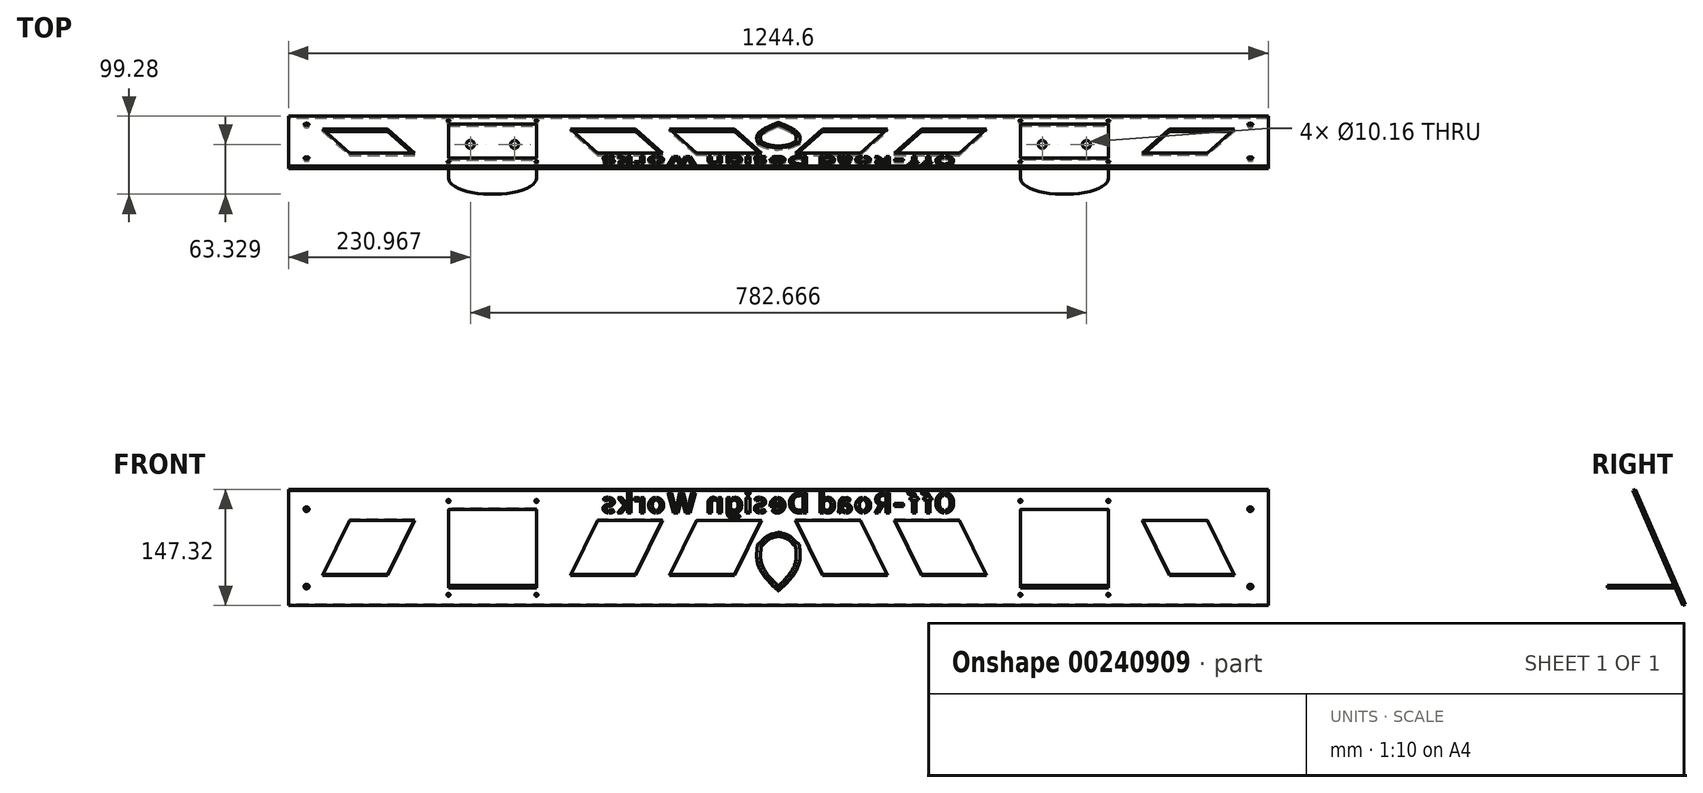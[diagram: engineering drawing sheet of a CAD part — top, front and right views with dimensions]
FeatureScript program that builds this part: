
annotation { "Feature Type Name" : "Feature", "Feature Type Description" : "" }
export const myFeature = defineFeature(function(context is Context, id is Id, definition is map)
    precondition{}
    {
        {
            var Q0;
            Q0=qCreatedBy(makeId("Right.planeOp"),FACE);
            var sketch = newSketch(context, id + "F0", { "sketchPlane" : qUnion([Q0])});
            skLineSegment(sketch, "E0", {"start": v(0, 0) * mm, "end": v(-63.5, 146.05) * mm});
            skLineSegment(sketch, "E1", {"start": v(-63.5, 146.05) * mm, "end": v(-66.41, 144.78) * mm});
            skLineSegment(sketch, "E2", {"start": v(-66.41, 144.78) * mm, "end": v(-2.91, -1.27) * mm});
            skLineSegment(sketch, "E3", {"start": v(-2.91, -1.27) * mm, "end": v(0, 0) * mm});
            skSolve(sketch);
        }
        {
            var Q0;
            Q0=qSketchRegion(id+"F0",true);
            extrude(context, id + "F1", {"entities" : qUnion([Q0]), "depth" : 622.3 * mm, "hasSecondDirection" : true, "secondDirectionOppositeDirection" : true, "secondDirectionDepth" : 622.3 * mm});
        }
        {
            var Q0;
            Q0=makeQuery(id+"F1.opExtrude","SWEPT_FACE",FACE,{"disambiguationData":[OSD([sQuery(id+"F0.wireOp",EDGE,"E0")])]});
            var sketch = newSketch(context, id + "F2", { "sketchPlane" : qUnion([Q0])});
            skSolve(sketch);
        }
        {
            var Q0;
            {var subQ0=sQuery(id+"F0.wireOp",EDGE,"E0");Q0=makeQuery(id+"F2.imprint","IMPRINT",FACE,{"disambiguationData":[TD([[makeQuery(id+"F2.imprint","IMPRINT",EDGE,{"derivedFrom":makeQuery(id+"F1.opExtrude","CAP_EDGE",EDGE,{"disambiguationData":[OSD([subQ0])],"isStart":true})}),1.0]])]});}
            var sketch = newSketch(context, id + "F3", { "sketchPlane" : qUnion([Q0])});
            skLineSegment(sketch, "E4", {"start": v(0, 0) * mm, "end": v(0, -192.6) * mm, "construction": true});
            skLineSegment(sketch, "E5", {"start": v(-307.34, 133.22) * mm, "end": v(-419.1, 133.22) * mm});
            skLineSegment(sketch, "E6", {"start": v(-419.1, 133.22) * mm, "end": v(-419.1, 26.03) * mm});
            skLineSegment(sketch, "E7", {"start": v(-419.1, 26.03) * mm, "end": v(-307.34, 26.03) * mm});
            skLineSegment(sketch, "E8", {"start": v(-307.34, 26.03) * mm, "end": v(-307.34, 133.22) * mm});
            skLineSegment(sketch, "E9", {"start": v(-462.28, 117.73) * mm, "end": v(-544.83, 117.73) * mm});
            skLineSegment(sketch, "E10", {"start": v(-544.83, 117.73) * mm, "end": v(-579.12, 41.53) * mm});
            skLineSegment(sketch, "E11", {"start": v(-579.12, 41.53) * mm, "end": v(-496.57, 41.53) * mm});
            skLineSegment(sketch, "E12", {"start": v(-496.57, 41.53) * mm, "end": v(-462.28, 117.73) * mm});
            skLineSegment(sketch, "E13", {"start": v(-229.87, 117.73) * mm, "end": v(-147.32, 117.73) * mm});
            skLineSegment(sketch, "E14", {"start": v(-147.32, 117.73) * mm, "end": v(-181.6, 41.53) * mm});
            skLineSegment(sketch, "E15", {"start": v(-181.6, 41.53) * mm, "end": v(-264.16, 41.53) * mm});
            skLineSegment(sketch, "E16", {"start": v(-264.16, 41.53) * mm, "end": v(-229.87, 117.73) * mm});
            skLineSegment(sketch, "E17.1.0.0", {"start": v(-21.59, 117.73) * mm, "end": v(-55.88, 41.53) * mm});
            skLineSegment(sketch, "E17.1.0.1", {"start": v(-55.88, 41.53) * mm, "end": v(-138.43, 41.53) * mm});
            skLineSegment(sketch, "E17.1.0.2", {"start": v(-138.43, 41.53) * mm, "end": v(-104.14, 117.73) * mm});
            skLineSegment(sketch, "E17.1.0.3", {"start": v(-104.14, 117.73) * mm, "end": v(-21.59, 117.73) * mm});
            skLineSegment(sketch, "E17.direction1", {"start": v(-229.87, 117.73) * mm, "end": v(-104.14, 117.73) * mm, "construction": true});
            skLineSegment(sketch, "E18.MirrorCS", {"start": v(104.14, 117.73) * mm, "end": v(21.59, 117.73) * mm});
            skLineSegment(sketch, "E19.MirrorCS", {"start": v(138.43, 41.53) * mm, "end": v(104.14, 117.73) * mm});
            skLineSegment(sketch, "E20.MirrorCS", {"start": v(21.59, 117.73) * mm, "end": v(55.88, 41.53) * mm});
            skLineSegment(sketch, "E21.MirrorCS", {"start": v(55.88, 41.53) * mm, "end": v(138.43, 41.53) * mm});
            skLineSegment(sketch, "E22.MirrorCS", {"start": v(147.32, 117.73) * mm, "end": v(181.6, 41.53) * mm});
            skLineSegment(sketch, "E23.MirrorCS", {"start": v(264.16, 41.53) * mm, "end": v(229.87, 117.73) * mm});
            skLineSegment(sketch, "E24.MirrorCS", {"start": v(229.87, 117.73) * mm, "end": v(104.14, 117.73) * mm, "construction": true});
            skLineSegment(sketch, "E25.MirrorCS", {"start": v(181.6, 41.53) * mm, "end": v(264.16, 41.53) * mm});
            skLineSegment(sketch, "E26.MirrorCS", {"start": v(419.1, 26.03) * mm, "end": v(307.34, 26.03) * mm});
            skLineSegment(sketch, "E27.MirrorCS", {"start": v(419.1, 133.22) * mm, "end": v(419.1, 26.03) * mm});
            skLineSegment(sketch, "E28.MirrorCS", {"start": v(307.34, 26.03) * mm, "end": v(307.34, 133.22) * mm});
            skLineSegment(sketch, "E29.MirrorCS", {"start": v(307.34, 133.22) * mm, "end": v(419.1, 133.22) * mm});
            skLineSegment(sketch, "E30.MirrorCS", {"start": v(496.57, 41.53) * mm, "end": v(462.28, 117.73) * mm});
            skLineSegment(sketch, "E31.MirrorCS", {"start": v(462.28, 117.73) * mm, "end": v(544.83, 117.73) * mm});
            skLineSegment(sketch, "E32.MirrorCS", {"start": v(544.83, 117.73) * mm, "end": v(579.12, 41.53) * mm});
            skLineSegment(sketch, "E33.MirrorCS", {"start": v(579.12, 41.53) * mm, "end": v(496.57, 41.53) * mm});
            skLineSegment(sketch, "E34", {"start": v(147.32, 117.73) * mm, "end": v(229.87, 117.73) * mm});
            skSolve(sketch);
        }
        {
            var Q0;
            Q0=qSketchRegion(id+"F3",true);
            var Q1;
            Q1=makeQuery(id+"F1.opExtrude","SWEPT_FACE",FACE,{"disambiguationData":[OSD([sQuery(id+"F0.wireOp",EDGE,"E2")])]});
            extrude(context, id + "F4", {"entities" : qUnion([Q0]), "operationType" : NewBodyOperationType.REMOVE, "endBound" : BoundingType.UP_TO_SURFACE, "oppositeDirection" : true, "endBoundEntityFace" : qUnion([Q1]), "depth" : 25.4 * mm});
        }
        {
            var Q0;
            {var subQ0=sQuery(id+"F0.wireOp",EDGE,"E0");Q0=makeQuery(id+"F2.imprint","IMPRINT",FACE,{"disambiguationData":[TD([[makeQuery(id+"F2.imprint","IMPRINT",EDGE,{"derivedFrom":makeQuery(id+"F1.opExtrude","CAP_EDGE",EDGE,{"disambiguationData":[OSD([subQ0])],"isStart":true})}),1.0]])]});}
            var sketch = newSketch(context, id + "F5", { "sketchPlane" : qUnion([Q0])});
            skCircle(sketch, "E35", {"center": v(-419.1, 144.65) * mm, "radius": 1.9 * mm});
            skCircle(sketch, "E36", {"center": v(-307.34, 144.65) * mm, "radius": 1.9 * mm});
            skCircle(sketch, "E37", {"center": v(-419.1, 14.6) * mm, "radius": 1.9 * mm});
            skCircle(sketch, "E38", {"center": v(-307.34, 14.6) * mm, "radius": 1.9 * mm});
            skLineSegment(sketch, "E39", {"start": v(0, 0) * mm, "end": v(0, -78.26) * mm, "construction": true});
            skCircle(sketch, "E40.MirrorC", {"center": v(307.34, 144.65) * mm, "radius": 1.9 * mm});
            skCircle(sketch, "E41.MirrorC", {"center": v(419.1, 144.65) * mm, "radius": 1.9 * mm});
            skCircle(sketch, "E42.MirrorC", {"center": v(419.1, 14.6) * mm, "radius": 1.9 * mm});
            skCircle(sketch, "E43.MirrorC", {"center": v(307.34, 14.6) * mm, "radius": 1.9 * mm});
            skCircle(sketch, "E44", {"center": v(-599.44, 133.22) * mm, "radius": 3.18 * mm});
            skCircle(sketch, "E45", {"center": v(-599.44, 26.03) * mm, "radius": 3.18 * mm});
            skCircle(sketch, "E46.MirrorC", {"center": v(599.44, 26.03) * mm, "radius": 3.18 * mm});
            skCircle(sketch, "E47.MirrorC", {"center": v(599.44, 133.22) * mm, "radius": 3.18 * mm});
            skSolve(sketch);
        }
        {
            var Q0;
            Q0=qSketchRegion(id+"F5",true);
            var Q1;
            Q1=makeQuery(id+"F1.opExtrude","SWEPT_FACE",FACE,{"disambiguationData":[OSD([sQuery(id+"F0.wireOp",EDGE,"E2")])]});
            extrude(context, id + "F6", {"entities" : qUnion([Q0]), "operationType" : NewBodyOperationType.REMOVE, "endBound" : BoundingType.UP_TO_SURFACE, "oppositeDirection" : true, "endBoundEntityFace" : qUnion([Q1]), "depth" : 25.4 * mm});
        }
        {
            var Q0;
            {var subQ0=sQuery(id+"F0.wireOp",EDGE,"E0");Q0=makeQuery(id+"F2.imprint","IMPRINT",FACE,{"disambiguationData":[TD([[makeQuery(id+"F2.imprint","IMPRINT",EDGE,{"derivedFrom":makeQuery(id+"F1.opExtrude","CAP_EDGE",EDGE,{"disambiguationData":[OSD([subQ0])],"isStart":true})}),1.0]])]});}
            var sketch = newSketch(context, id + "F7", { "sketchPlane" : qUnion([Q0])});
            skText(sketch, "E48", { "text": "Off-Road Design Works", "fontName": "AllertaStencil-Regular.ttf"});
            skLineSegment(sketch, "E49", {"start": v(0, 128.23) * mm, "end": v(0, 0) * mm, "construction": true});
            const initialGuessF7  = {"E48": [-0.22543, 0.12823, 1, 0, 0.02722]};
            skSetInitialGuess(sketch, initialGuessF7);
            skSolve(sketch);
        }
        {
            var Q0;
            Q0=qSketchRegion(id+"F7",true);
            var Q1;
            Q1=makeQuery(id+"F1.opExtrude","SWEPT_FACE",FACE,{"disambiguationData":[OSD([sQuery(id+"F0.wireOp",EDGE,"E2")])]});
            extrude(context, id + "F8", {"entities" : qUnion([Q0]), "operationType" : NewBodyOperationType.REMOVE, "endBound" : BoundingType.UP_TO_SURFACE, "oppositeDirection" : true, "endBoundEntityFace" : qUnion([Q1]), "depth" : 25.4 * mm});
        }
        {
            var Q0;
            Q0=qCreatedBy(makeId("Top.planeOp"),FACE);
            var Q1;
            Q1=makeQuery(id+"F4.boolean.opBoolean","COPY",VERTEX,{"derivedFrom":makeQuery(id+"F4.opExtrude","CAP_VERTEX",VERTEX,{"disambiguationData":[OSD([sQuery(id+"F3.wireOp",EDGE,"E7"),sQuery(id+"F3.wireOp",EDGE,"E8")])],"isStart":true})});
            cPlane(context, id + "F9", {"entities" : qUnion([Q0, Q1]), "cplaneType" : CPlaneType.PLANE_POINT, "offset" : 25.4 * mm, "width" : 152.4 * mm, "height" : 152.4 * mm});
        }
        {
            var Q0;
            Q0=qCreatedBy(id+"F9.planeOp",FACE);
            var sketch = newSketch(context, id + "F10", { "sketchPlane" : qUnion([Q0])});
            skLineSegment(sketch, "E50", {"start": v(419.1, -10.38) * mm, "end": v(419.1, -78.96) * mm});
            skLineSegment(sketch, "E51", {"start": v(307.34, -10.38) * mm, "end": v(307.34, -78.96) * mm});
            skLineSegment(sketch, "E52", {"start": v(363.22, -11.11) * mm, "end": v(363.22, -61.05) * mm, "construction": true});
            skEllipticalArc(sketch, "E53", {});
            skLineSegment(sketch, "E54", {"start": v(307.34, -10.38) * mm, "end": v(419.1, -10.38) * mm});
            skLineSegment(sketch, "E55", {"start": v(0, 0) * mm, "end": v(0, -97.93) * mm, "construction": true});
            skLineSegment(sketch, "E56.MirrorCS", {"start": v(-307.34, -10.38) * mm, "end": v(-307.34, -78.96) * mm});
            skLineSegment(sketch, "E57.MirrorCS", {"start": v(-307.34, -10.38) * mm, "end": v(-419.1, -10.38) * mm});
            skLineSegment(sketch, "E58.MirrorCS", {"start": v(-419.1, -10.38) * mm, "end": v(-419.1, -78.96) * mm});
            skEllipticalArc(sketch, "E59.MirrorCS", {});
            skCircle(sketch, "E60", {"center": v(391.33, -35.95) * mm, "radius": 5.08 * mm});
            skCircle(sketch, "E61.MirrorC", {"center": v(335.1, -35.95) * mm, "radius": 5.08 * mm});
            skCircle(sketch, "E62.MirrorC", {"center": v(-335.1, -35.95) * mm, "radius": 5.08 * mm});
            skCircle(sketch, "E63.MirrorC", {"center": v(-391.33, -35.95) * mm, "radius": 5.08 * mm});
            const initialGuessF10  = {"E53": [0.36322, -0.07896051125903271, 1, 0, 0.05588, 0.02032, 3.141592653589793, 0], "E59.MirrorCS": [-0.36322, -0.07896051125903271, -1, 0, 0.05588, 0.02032, 0, 3.141592653589793]};
            skSetInitialGuess(sketch, initialGuessF10);
            skSolve(sketch);
        }
        {
            var Q0;
            Q0=qSketchRegion(id+"F10",true);
            extrude(context, id + "F11", {"entities" : qUnion([Q0]), "operationType" : NewBodyOperationType.ADD, "oppositeDirection" : true, "depth" : 3.17 * mm});
        }
        {
            var Q0;
            {var subQ0=sQuery(id+"F0.wireOp",EDGE,"E0");Q0=makeQuery(id+"F2.imprint","IMPRINT",FACE,{"disambiguationData":[TD([[makeQuery(id+"F2.imprint","IMPRINT",EDGE,{"derivedFrom":makeQuery(id+"F1.opExtrude","CAP_EDGE",EDGE,{"disambiguationData":[OSD([subQ0])],"isStart":true})}),1.0]])]});}
            var sketch = newSketch(context, id + "F12", { "sketchPlane" : qUnion([Q0])});
            skLineSegment(sketch, "E64", {"start": v(0, 0) * mm, "end": v(0, 201.67) * mm, "construction": true});
            skFitSpline(sketch, "E65", {"points": [v(0, 20.03) * mm, v(-26.56, 84.7) * mm], "startDerivative": vector(-94.3, 90.63) * mm, "endDerivative": vector(5.61, 60.71) * mm});
            skFitSpline(sketch, "E66", {"points": [v(-26.56, 84.7) * mm, v(0, 100.83) * mm], "startDerivative": vector(26.56, 16.14) * mm, "endDerivative": vector(61.74, 11.54) * mm});
            skFitSpline(sketch, "E67.MirrorCS", {"points": [v(0, 20.03) * mm, v(26.56, 84.7) * mm], "startDerivative": vector(94.3, 90.63) * mm, "endDerivative": vector(-5.61, 60.71) * mm});
            skFitSpline(sketch, "E68.MirrorCS", {"points": [v(26.56, 84.7) * mm, v(0, 100.83) * mm], "startDerivative": vector(-26.56, 16.14) * mm, "endDerivative": vector(-61.74, 11.54) * mm});
            skFitSpline(sketch, "E69.0", {"points": [v(23.92, 80.35) * mm, v(23.24, 80.77) * mm, v(21.97, 81.62) * mm, v(20.33, 82.96) * mm, v(18.93, 84.3) * mm, v(17.74, 85.6) * mm, v(16.72, 86.8) * mm, v(15.81, 87.88) * mm, v(14.97, 88.84) * mm, v(14.14, 89.7) * mm, v(13.26, 90.5) * mm, v(12.26, 91.28) * mm, v(11.04, 92.05) * mm, v(9.02, 93.1) * mm, v(5.57, 94.4) * mm, v(1.5, 95.39) * mm, v(-0.93, 95.84) * mm]});
            skFitSpline(sketch, "E69.1", {"points": [v(-3.52, 23.7) * mm, v(0.32, 27.38) * mm, v(6.9, 34.24) * mm, v(13.91, 43.13) * mm, v(18.48, 50.85) * mm, v(21.14, 57.64) * mm, v(22.39, 63.92) * mm, v(22.65, 70.18) * mm, v(22.24, 76.81) * mm, v(21.74, 81.66) * mm, v(21.5, 84.22) * mm]});
            skFitSpline(sketch, "E69.2", {"points": [v(3.52, 23.7) * mm, v(-0.32, 27.38) * mm, v(-6.9, 34.24) * mm, v(-13.91, 43.13) * mm, v(-18.48, 50.85) * mm, v(-21.14, 57.64) * mm, v(-22.39, 63.92) * mm, v(-22.65, 70.18) * mm, v(-22.24, 76.81) * mm, v(-21.74, 81.66) * mm, v(-21.5, 84.22) * mm]});
            skFitSpline(sketch, "E69.3", {"points": [v(-23.92, 80.35) * mm, v(-23.24, 80.77) * mm, v(-21.97, 81.62) * mm, v(-20.33, 82.96) * mm, v(-18.93, 84.3) * mm, v(-17.74, 85.6) * mm, v(-16.72, 86.8) * mm, v(-15.81, 87.88) * mm, v(-14.97, 88.84) * mm, v(-14.14, 89.7) * mm, v(-13.26, 90.5) * mm, v(-12.26, 91.28) * mm, v(-11.04, 92.05) * mm, v(-9.02, 93.1) * mm, v(-5.57, 94.4) * mm, v(-1.5, 95.39) * mm, v(0.93, 95.84) * mm]});
            skLineSegment(sketch, "E70", {"start": v(4.83, 99.77) * mm, "end": v(4.83, 94.5) * mm});
            skLineSegment(sketch, "E71.MirrorCS", {"start": v(-4.83, 99.77) * mm, "end": v(-4.83, 94.5) * mm});
            skLineSegment(sketch, "E72.trimOffspring", {"start": v(4.83, 32.22) * mm, "end": v(4.83, 24.82) * mm});
            skLineSegment(sketch, "E73.trimOffspring", {"start": v(-4.83, 32.22) * mm, "end": v(-4.83, 24.82) * mm});
            skText(sketch, "E74", { "text": "OD", "fontName": "AllertaStencil-Regular.ttf"});
            skText(sketch, "E75", { "text": "W", "fontName": "AllertaStencil-Regular.ttf"});
            const initialGuessF12  = {"E74": [-0.01742, 0.06557, 1, 0, 0.01682], "E75": [-0.01143, 0.04464, 1, 0, 0.01545]};
            skSetInitialGuess(sketch, initialGuessF12);
            skSolve(sketch);
        }
        {
            var Q0;
            Q0=qSketchRegion(id+"F12",true);
            var Q1;
            Q1=makeQuery(id+"F1.opExtrude","SWEPT_FACE",FACE,{"disambiguationData":[OSD([sQuery(id+"F0.wireOp",EDGE,"E2")])]});
            extrude(context, id + "F13", {"entities" : qUnion([Q0]), "operationType" : NewBodyOperationType.REMOVE, "endBound" : BoundingType.UP_TO_SURFACE, "oppositeDirection" : true, "endBoundEntityFace" : qUnion([Q1]), "depth" : 25.4 * mm});
        }
    });
